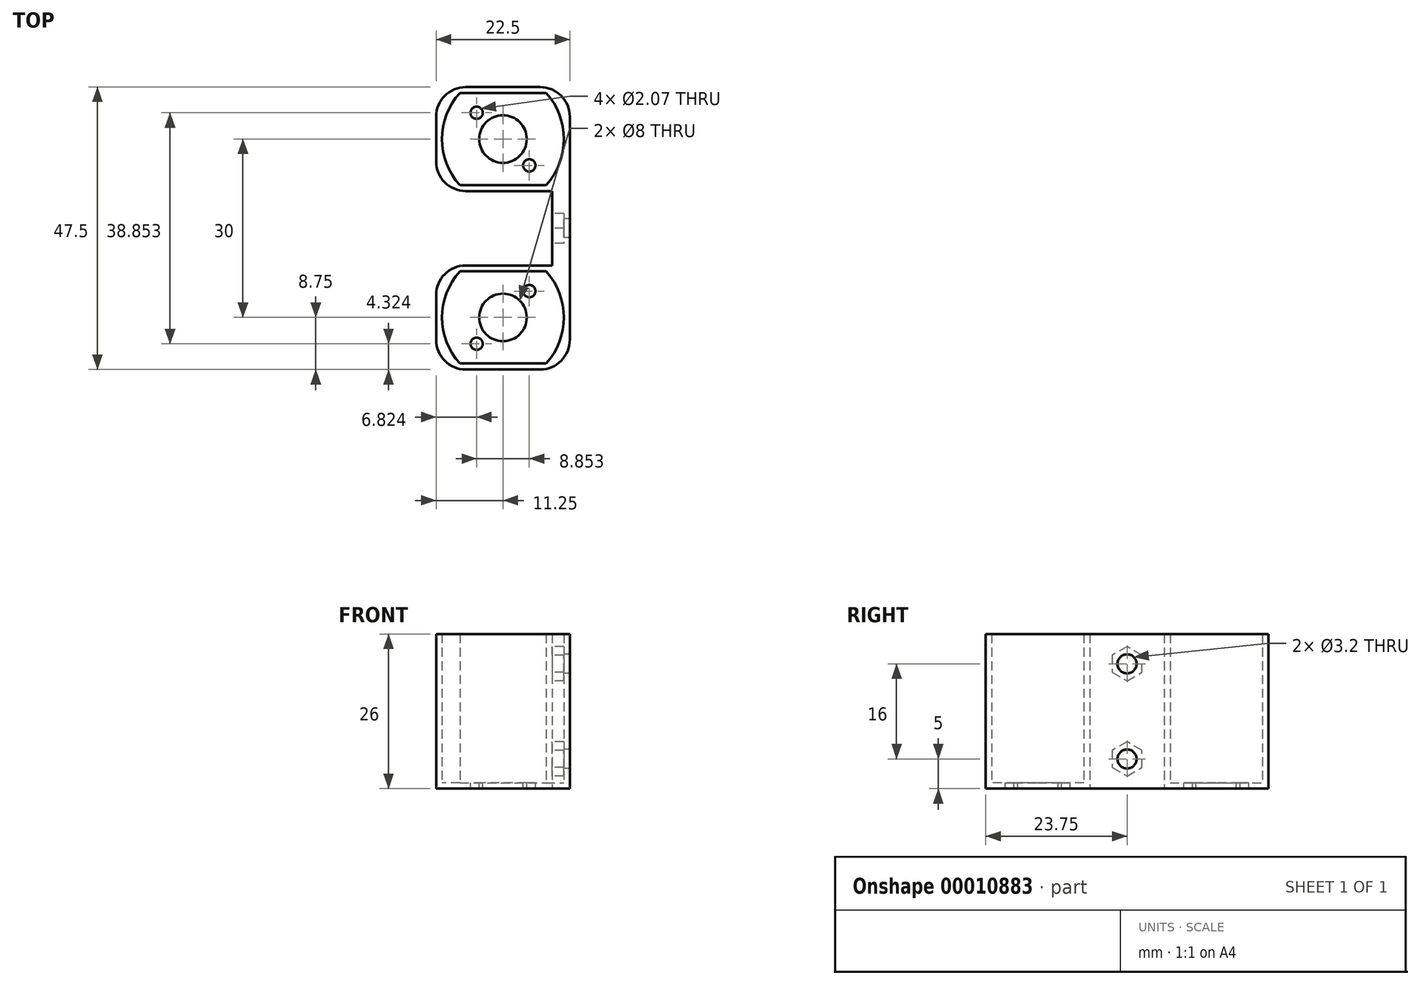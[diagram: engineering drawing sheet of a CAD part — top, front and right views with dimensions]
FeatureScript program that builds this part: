
annotation { "Feature Type Name" : "Feature", "Feature Type Description" : "" }
export const myFeature = defineFeature(function(context is Context, id is Id, definition is map)
    precondition{}
    {
        {
            var Q0;
            Q0=qCreatedBy(makeId("Top.planeOp"),FACE);
            var sketch = newSketch(context, id + "F0", { "sketchPlane" : qUnion([Q0])});
            skLineSegment(sketch, "E0.bottom", {"start": v(-7.25, 7.75) * mm, "end": v(7.25, 7.75) * mm});
            skLineSegment(sketch, "E0.top", {"start": v(-7.25, -7.75) * mm, "end": v(7.25, -7.75) * mm});
            skLineSegment(sketch, "E0.left", {"start": v(-7.25, 7.75) * mm, "end": v(-7.25, -7.75) * mm, "construction": true});
            skLineSegment(sketch, "E0.right", {"start": v(7.25, 7.75) * mm, "end": v(7.25, -7.75) * mm, "construction": true});
            skArc(sketch, "E1", {"start": v(-7.25, 7.75) * mm, "mid": v(-10.25, 0) * mm, "end": v(-7.25, -7.75) * mm});
            skArc(sketch, "E2", {"start": v(7.25, -7.75) * mm, "mid": v(10.25, 0) * mm, "end": v(7.25, 7.75) * mm});
            skLineSegment(sketch, "E3", {"start": v(-7.25, 7.75) * mm, "end": v(-10.25, 7.75) * mm, "construction": true});
            skLineSegment(sketch, "E4", {"start": v(-10.25, 7.75) * mm, "end": v(-10.25, -7.75) * mm, "construction": true});
            skLineSegment(sketch, "E5", {"start": v(-10.25, -7.75) * mm, "end": v(-7.25, -7.75) * mm, "construction": true});
            skLineSegment(sketch, "E6", {"start": v(7.25, -7.75) * mm, "end": v(10.25, -7.75) * mm, "construction": true});
            skLineSegment(sketch, "E7", {"start": v(10.25, -7.75) * mm, "end": v(10.25, 7.75) * mm, "construction": true});
            skLineSegment(sketch, "E8", {"start": v(10.25, 7.75) * mm, "end": v(7.25, 7.75) * mm, "construction": true});
            skLineSegment(sketch, "E9.bottom", {"start": v(-11.25, 8.75) * mm, "end": v(11.25, 8.75) * mm});
            skLineSegment(sketch, "E9.top", {"start": v(-11.25, -8.75) * mm, "end": v(11.25, -8.75) * mm});
            skLineSegment(sketch, "E9.left", {"start": v(-11.25, 8.75) * mm, "end": v(-11.25, -8.75) * mm});
            skLineSegment(sketch, "E9.right", {"start": v(11.25, 8.75) * mm, "end": v(11.25, -8.75) * mm});
            skPoint(sketch, "E10.visualSharp", {"position": v(-11.25, 8.75) * mm});
            skPoint(sketch, "E11.visualSharp", {"position": v(11.25, 8.75) * mm});
            skPoint(sketch, "E12.visualSharp", {"position": v(11.25, -8.75) * mm});
            skPoint(sketch, "E13.visualSharp", {"position": v(-11.25, -8.75) * mm});
            skLineSegment(sketch, "E14", {"start": v(-1.26, 0) * mm, "end": v(1.26, 0) * mm, "construction": true});
            skPoint(sketch, "E15", {"position": v(0, 0) * mm});
            skLineSegment(sketch, "E16", {"start": v(10.25, -7.75) * mm, "end": v(10.25, -8.75) * mm, "construction": true});
            skLineSegment(sketch, "E17", {"start": v(-10.25, 7.75) * mm, "end": v(-10.25, 8.75) * mm, "construction": true});
            skLineSegment(sketch, "E18", {"start": v(-10.25, 7.75) * mm, "end": v(-11.25, 7.75) * mm, "construction": true});
            skLineSegment(sketch, "E19", {"start": v(10.25, -7.75) * mm, "end": v(11.25, -7.75) * mm, "construction": true});
            skSolve(sketch);
        }
        {
            var Q0;
            Q0=qSketchRegion(id+"F0",true);
            extrude(context, id + "F1", {"entities" : qUnion([Q0]), "depth" : 25 * mm});
        }
        {
            var Q0;
            Q0=qCreatedBy(makeId("Top.planeOp"),FACE);
            var sketch = newSketch(context, id + "F2", { "sketchPlane" : qUnion([Q0])});
            skCircle(sketch, "E20", {"center": v(0, 0) * mm, "radius": 4 * mm});
            skLineSegment(sketch, "E21", {"start": v(-4.43, -4.43) * mm, "end": v(4.43, 4.43) * mm, "construction": true});
            skCircle(sketch, "E22", {"center": v(-4.43, -4.43) * mm, "radius": 1.04 * mm});
            skCircle(sketch, "E23", {"center": v(4.43, 4.43) * mm, "radius": 1.04 * mm});
            skLineSegment(sketch, "E24", {"start": v(0, 0) * mm, "end": v(0, -4) * mm, "construction": true});
            skLineSegment(sketch, "E25.bottom", {"start": v(-11.25, -8.75) * mm, "end": v(11.25, -8.75) * mm});
            skLineSegment(sketch, "E25.top", {"start": v(-11.25, 8.75) * mm, "end": v(11.25, 8.75) * mm});
            skLineSegment(sketch, "E25.left", {"start": v(-11.25, -8.75) * mm, "end": v(-11.25, 8.75) * mm});
            skLineSegment(sketch, "E25.right", {"start": v(11.25, -8.75) * mm, "end": v(11.25, 8.75) * mm});
            skSolve(sketch);
        }
        {
            var Q0;
            Q0=qSketchRegion(id+"F2",true);
            extrude(context, id + "F3", {"entities" : qUnion([Q0]), "operationType" : NewBodyOperationType.ADD, "oppositeDirection" : true, "depth" : 1 * mm});
        }
        {
            var Q0;
            Q0=makeQuery(id+"F3.boolean.opBoolean","MERGE",EDGE,{"derivedFrom":[makeQuery(id+"F1.opExtrude","SWEPT_EDGE",EDGE,{"disambiguationData":[OSD([sQuery(id+"F0.wireOp",EDGE,"E9.bottom"),sQuery(id+"F0.wireOp",EDGE,"E9.left")])]}),makeQuery(id+"F3.opExtrude","SWEPT_EDGE",EDGE,{"disambiguationData":[OSD([sQuery(id+"F2.wireOp",EDGE,"E25.top"),sQuery(id+"F2.wireOp",EDGE,"E25.left")])]})]});
            var Q1;
            Q1=makeQuery(id+"F3.boolean.opBoolean","MERGE",EDGE,{"derivedFrom":[makeQuery(id+"F1.opExtrude","SWEPT_EDGE",EDGE,{"disambiguationData":[OSD([sQuery(id+"F0.wireOp",EDGE,"E9.top"),sQuery(id+"F0.wireOp",EDGE,"E9.left")])]}),makeQuery(id+"F3.opExtrude","SWEPT_EDGE",EDGE,{"disambiguationData":[OSD([sQuery(id+"F2.wireOp",EDGE,"E25.bottom"),sQuery(id+"F2.wireOp",EDGE,"E25.left")])]})]});
            var Q2;
            Q2=makeQuery(id+"F3.boolean.opBoolean","MERGE",EDGE,{"derivedFrom":[makeQuery(id+"F1.opExtrude","SWEPT_EDGE",EDGE,{"disambiguationData":[OSD([sQuery(id+"F0.wireOp",EDGE,"E9.top"),sQuery(id+"F0.wireOp",EDGE,"E9.right")])]}),makeQuery(id+"F3.opExtrude","SWEPT_EDGE",EDGE,{"disambiguationData":[OSD([sQuery(id+"F2.wireOp",EDGE,"E25.bottom"),sQuery(id+"F2.wireOp",EDGE,"E25.right")])]})]});
            fillet(context, id + "F4", {"entities" : qUnion([Q0, Q1, Q2]), "radius" : 5 * mm, "tangentPropagation" : true, "allowEdgeOverflow" : false});
        }
        {
            var Q0;
            Q0=makeQuery(id+"F3.opExtrude","CAP_FACE",FACE,{"disambiguationData":[OSD([sQuery(id+"F2.wireOp",EDGE,"E20"),sQuery(id+"F2.wireOp",EDGE,"E22"),sQuery(id+"F2.wireOp",EDGE,"E23"),sQuery(id+"F2.wireOp",EDGE,"E25.bottom"),sQuery(id+"F2.wireOp",EDGE,"E25.top"),sQuery(id+"F2.wireOp",EDGE,"E25.left"),sQuery(id+"F2.wireOp",EDGE,"E25.right")])],"isStart":false});
            var sketch = newSketch(context, id + "F5", { "sketchPlane" : qUnion([Q0])});
            skLineSegment(sketch, "E26.bottom", {"start": v(11.25, -8.75) * mm, "end": v(8.25, -8.75) * mm});
            skLineSegment(sketch, "E26.top", {"start": v(11.25, -15) * mm, "end": v(8.25, -15) * mm});
            skLineSegment(sketch, "E26.left", {"start": v(11.25, -8.75) * mm, "end": v(11.25, -15) * mm});
            skLineSegment(sketch, "E26.right", {"start": v(8.25, -8.75) * mm, "end": v(8.25, -15) * mm});
            skSolve(sketch);
        }
        {
            var Q0;
            Q0=qSketchRegion(id+"F5",true);
            var Q1;
            Q1=makeQuery(id+"F1.opExtrude","CAP_FACE",FACE,{"disambiguationData":[OSD([sQuery(id+"F0.wireOp",EDGE,"E0.bottom"),sQuery(id+"F0.wireOp",EDGE,"E0.top"),sQuery(id+"F0.wireOp",EDGE,"E1"),sQuery(id+"F0.wireOp",EDGE,"E2"),sQuery(id+"F0.wireOp",EDGE,"E9.bottom"),sQuery(id+"F0.wireOp",EDGE,"E9.top"),sQuery(id+"F0.wireOp",EDGE,"E9.left"),sQuery(id+"F0.wireOp",EDGE,"E9.right")])],"isStart":false});
            extrude(context, id + "F6", {"entities" : qUnion([Q0]), "operationType" : NewBodyOperationType.ADD, "endBound" : BoundingType.UP_TO_SURFACE, "oppositeDirection" : true, "endBoundEntityFace" : qUnion([Q1]), "depth" : 5 * mm});
        }
        {
            var Q0;
            Q0=makeQuery(id+"F1.opExtrude","SWEPT_BODY",BODY,{"disambiguationData":[OSD([sQuery(id+"F0.wireOp",EDGE,"E0.bottom"),sQuery(id+"F0.wireOp",EDGE,"E0.top"),sQuery(id+"F0.wireOp",EDGE,"E1"),sQuery(id+"F0.wireOp",EDGE,"E2"),sQuery(id+"F0.wireOp",EDGE,"E9.bottom"),sQuery(id+"F0.wireOp",EDGE,"E9.top"),sQuery(id+"F0.wireOp",EDGE,"E9.left"),sQuery(id+"F0.wireOp",EDGE,"E9.right")])]});
            var Q1;
            Q1=makeQuery(id+"F6.opExtrude","SWEPT_FACE",FACE,{"disambiguationData":[OSD([sQuery(id+"F5.wireOp",EDGE,"E26.top")])]});
            mirror(context, id + "F7", {"operationType" : NewBodyOperationType.ADD, "entities" : qUnion([Q0]), "mirrorPlane" : qUnion([Q1])});
        }
        {
            var Q0;
            {var subQ0=makeQuery(id+"F6.opExtrude","SWEPT_FACE",FACE,{"disambiguationData":[OSD([sQuery(id+"F5.wireOp",EDGE,"E26.right")])]});Q0=makeQuery(id+"F7.boolean.opBoolean","MERGE",FACE,{"derivedFrom":[subQ0,makeQuery(id+"F7.opPattern","COPY",FACE,{"derivedFrom":subQ0,"instanceName":"1"})]});}
            var sketch = newSketch(context, id + "F8", { "sketchPlane" : qUnion([Q0])});
            skLineSegment(sketch, "E27", {"start": v(-15, -1) * mm, "end": v(-15, 4) * mm, "construction": true});
            skLineSegment(sketch, "E28", {"start": v(-15, 4) * mm, "end": v(-15, 20) * mm, "construction": true});
            skLineSegment(sketch, "E29", {"start": v(-15, 20) * mm, "end": v(-15, 25) * mm, "construction": true});
            skCircle(sketch, "E30.cCircle", {"center": v(-15, 4) * mm, "radius": 2.5 * mm, "construction": true});
            skLineSegment(sketch, "E30.0", {"start": v(-17.5, 2.56) * mm, "end": v(-17.5, 5.44) * mm});
            skLineSegment(sketch, "E30.1", {"start": v(-17.5, 5.44) * mm, "end": v(-15, 6.89) * mm});
            skLineSegment(sketch, "E30.2", {"start": v(-15, 6.89) * mm, "end": v(-12.5, 5.44) * mm});
            skLineSegment(sketch, "E30.3", {"start": v(-12.5, 5.44) * mm, "end": v(-12.5, 2.56) * mm});
            skLineSegment(sketch, "E30.4", {"start": v(-12.5, 2.56) * mm, "end": v(-15, 1.11) * mm});
            skLineSegment(sketch, "E30.5", {"start": v(-15, 1.11) * mm, "end": v(-17.5, 2.56) * mm});
            skPoint(sketch, "E30.0.midPoint", {"position": v(-17.5, 4) * mm});
            skCircle(sketch, "E31.cCircle", {"center": v(-15, 20) * mm, "radius": 2.5 * mm, "construction": true});
            skLineSegment(sketch, "E31.0", {"start": v(-15, 22.89) * mm, "end": v(-12.5, 21.44) * mm});
            skLineSegment(sketch, "E31.1", {"start": v(-12.5, 21.44) * mm, "end": v(-12.5, 18.56) * mm});
            skLineSegment(sketch, "E31.2", {"start": v(-12.5, 18.56) * mm, "end": v(-15, 17.11) * mm});
            skLineSegment(sketch, "E31.3", {"start": v(-15, 17.11) * mm, "end": v(-17.5, 18.56) * mm});
            skLineSegment(sketch, "E31.4", {"start": v(-17.5, 18.56) * mm, "end": v(-17.5, 21.44) * mm});
            skLineSegment(sketch, "E31.5", {"start": v(-17.5, 21.44) * mm, "end": v(-15, 22.89) * mm});
            skPoint(sketch, "E31.0.midPoint", {"position": v(-13.75, 22.17) * mm});
            skSolve(sketch);
        }
        {
            var Q0;
            Q0 = qSketchRegion(id + "F8", true);
            extrude(context, id + "F9", {"entities" : qUnion([Q0]), "operationType" : NewBodyOperationType.REMOVE, "oppositeDirection" : true, "depth" : 2 * mm});
        }
        {
            var Q0;
            Q0=makeQuery(id+"F8.imprint","IMPRINT",FACE,{"disambiguationData":[TD([[makeQuery(id+"F8.imprint","IMPRINT",EDGE,{"derivedFrom":sQuery(id+"F8.wireOp",EDGE,"E30.0")}),1.0]])]});
            var sketch = newSketch(context, id + "F10", { "sketchPlane" : qUnion([Q0])});
            skCircle(sketch, "E32", {"center": v(-15, 4) * mm, "radius": 1.6 * mm});
            skCircle(sketch, "E33", {"center": v(-15, 20) * mm, "radius": 1.6 * mm});
            skSolve(sketch);
        }
        {
            var Q0;
            Q0 = qSketchRegion(id + "F10", true);
            extrude(context, id + "F11", {"entities" : qUnion([Q0]), "operationType" : NewBodyOperationType.REMOVE, "endBound" : BoundingType.THROUGH_ALL, "oppositeDirection" : true, "depth" : 25 * mm});
        }
    });
